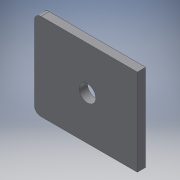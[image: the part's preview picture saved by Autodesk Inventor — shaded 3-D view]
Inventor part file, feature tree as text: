
AUTODESK INVENTOR PART (.ipt)
format: ipt  version: 2019 (Build 230136000, 136)  size: 137,728 bytes
history: native  units: in
note: dims shown in document units (in); Inventor stores cm internally (conversion verified against a paired STEP export)
features: reference x7, other x4, extrude x2, sketch x2, fillet x1, helix x1
ambient origin geometry x8: Origin, YZ Plane, XZ Plane, XY Plane, X Axis, Y Axis, Z Axis, Center Point
bodies: Solid1 (feature_tree)
feature tree (17):
  extrude  "Extrusion1"  Depth=0.1575in TaperAngle=0.0deg
  fillet  "Fillet1"  Radius=0.125in
  extrude  "Extrusion2"  Depth=0.1575in
  sketch  "Sketch1"  dims[d0=0.315in d1=0.1575in d2=0.0in d3=0.125in]
  reference  "Reference1"
  sketch  "Sketch2"  dims[d4=0.0079in d5=0.0079in d6=0.0079in d7=0.0079in d8=0.126in d9=0.126in d10=0.1575in d11=0.0in]
  reference  "Reference2"
  reference  "Reference3"
  reference  "Reference4"
  reference  "Reference5"
  reference  "Reference6"
  reference  "Reference7"
  other  "<userpath>\Documents\CAD Files\Helix DLP\Helix DLP.iam"
  helix  "Helix DLP.iam"  [1 undecoded]
  other  "Z Motor Screw:1"
  other  "motor_brace_3:3"
  other  "motor_brace_3:4"
note: 1 required parameter value undecoded (feature->parameter linkage not recoverable at this tier; creation-order binding heuristic only, values carry confidence <= 0.55)
